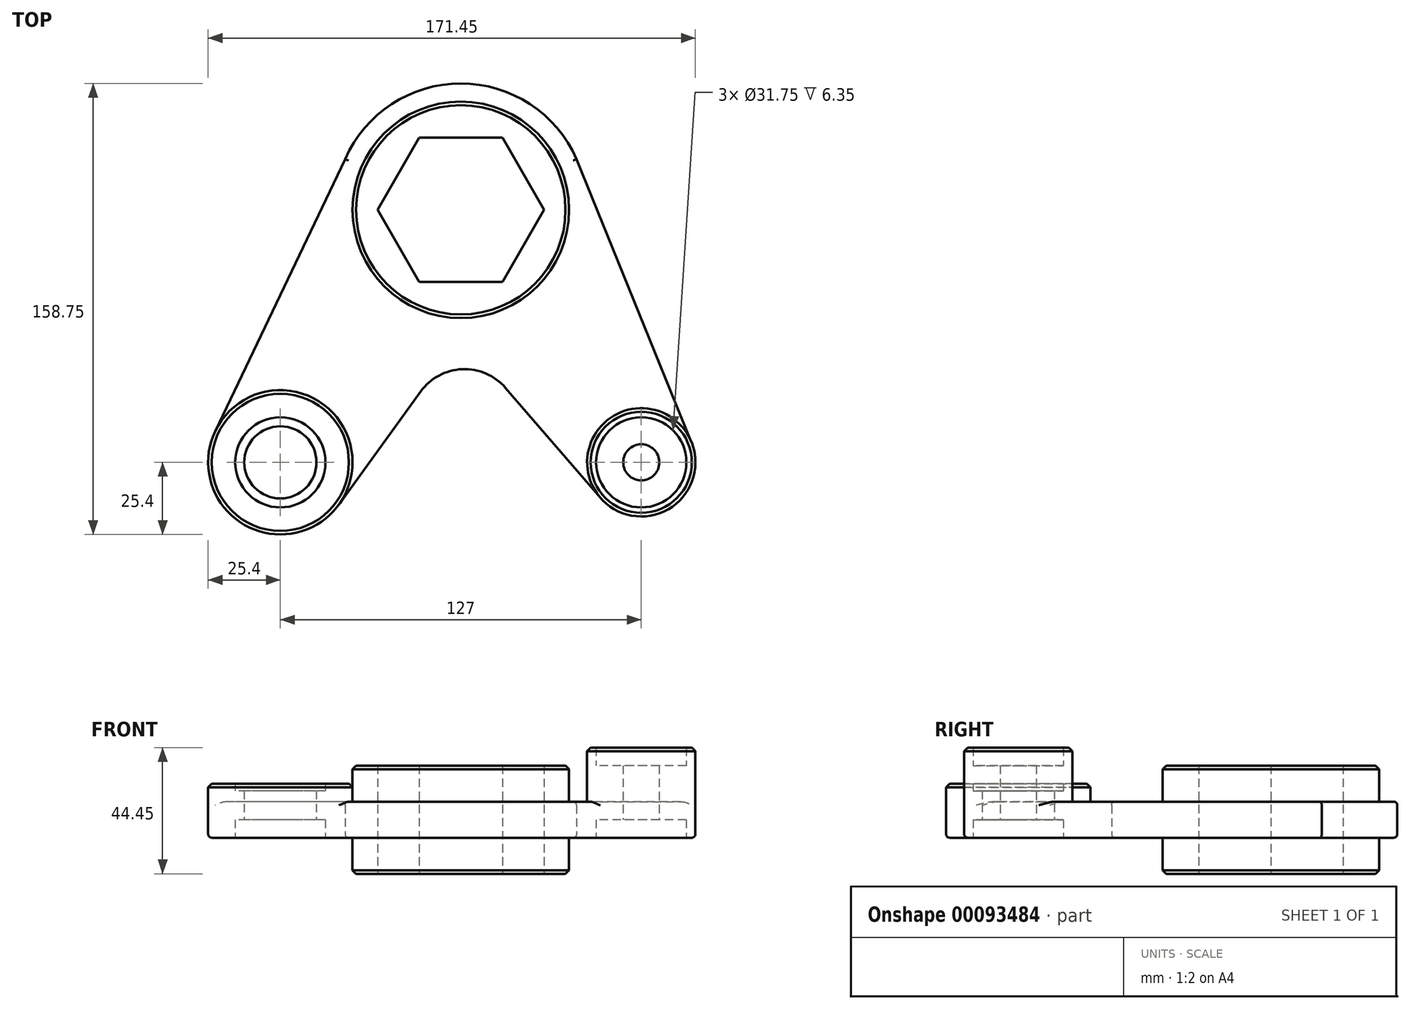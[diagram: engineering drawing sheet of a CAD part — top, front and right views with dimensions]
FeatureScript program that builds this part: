
annotation { "Feature Type Name" : "Feature", "Feature Type Description" : "" }
export const myFeature = defineFeature(function(context is Context, id is Id, definition is map)
    precondition{}
    {
        {
            var Q0;
            Q0=qCreatedBy(makeId("Top.planeOp"),FACE);
            var sketch = newSketch(context, id + "F0", { "sketchPlane" : qUnion([Q0])});
            skCircle(sketch, "E0", {"center": v(0, 0) * mm, "radius": 38.1 * mm});
            skCircle(sketch, "E1", {"center": v(0, 0) * mm, "radius": 44.45 * mm});
            skArc(sketch, "E2", {"start": v(-38.1, -88.9) * mm, "mid": v(-87.67, -81.08) * mm, "end": v(-42.92, -103.79) * mm});
            skCircle(sketch, "E3", {"center": v(63.5, -88.9) * mm, "radius": 19.05 * mm});
            skLineSegment(sketch, "E4", {"start": v(-40.71, 17.84) * mm, "end": v(-86.42, -77.96) * mm});
            skLineSegment(sketch, "E5", {"start": v(40.71, 17.84) * mm, "end": v(81.15, -81.73) * mm});
            skLineSegment(sketch, "E6", {"start": v(-14.12, -63.97) * mm, "end": v(-42.92, -103.79) * mm});
            skLineSegment(sketch, "E7", {"start": v(15.74, -62.7) * mm, "end": v(49.08, -101.34) * mm});
            skPoint(sketch, "E8.visualSharp", {"position": v(0, -44.45) * mm});
            skArc(sketch, "E8.filletArc", {"start": v(15.74, -62.7) * mm, "mid": v(0.5, -56.1) * mm, "end": v(-14.12, -63.97) * mm});
            skCircle(sketch, "E9.cCircle", {"center": v(0, 0) * mm, "radius": 25.4 * mm, "construction": true});
            skLineSegment(sketch, "E9.0", {"start": v(-14.66, 25.4) * mm, "end": v(14.66, 25.4) * mm});
            skLineSegment(sketch, "E9.1", {"start": v(14.66, 25.4) * mm, "end": v(29.33, 0) * mm});
            skLineSegment(sketch, "E9.2", {"start": v(29.33, 0) * mm, "end": v(14.66, -25.4) * mm});
            skLineSegment(sketch, "E9.3", {"start": v(14.66, -25.4) * mm, "end": v(-14.66, -25.4) * mm});
            skLineSegment(sketch, "E9.4", {"start": v(-14.66, -25.4) * mm, "end": v(-29.33, 0) * mm});
            skLineSegment(sketch, "E9.5", {"start": v(-29.33, 0) * mm, "end": v(-14.66, 25.4) * mm});
            skPoint(sketch, "E9.0.midPoint", {"position": v(0, 25.4) * mm});
            skCircle(sketch, "E10", {"center": v(63.5, -88.9) * mm, "radius": 6.35 * mm});
            skCircle(sketch, "E11", {"center": v(63.5, -88.9) * mm, "radius": 15.88 * mm});
            skCircle(sketch, "E12", {"center": v(-63.5, -88.9) * mm, "radius": 12.7 * mm});
            skCircle(sketch, "E13", {"center": v(-63.5, -88.9) * mm, "radius": 15.88 * mm});
            skArc(sketch, "E14", {"start": v(-86.42, -77.96) * mm, "mid": v(-69.1, -113.67) * mm, "end": v(-38.1, -88.9) * mm});
            skSolve(sketch);
        }
        {
            var Q0;
            {var subQ0=sQuery(id+"F0.wireOp",EDGE,"E4");Q0=makeQuery(id+"F0.imprint","IMPRINT",FACE,{"disambiguationData":[TD([[makeQuery(id+"F0.imprint","IMPRINT",EDGE,{"derivedFrom":subQ0}),1.0]])]});}
            var Q1;
            {var subQ0=sQuery(id+"F0.wireOp",EDGE,"E2");var subQ1=makeQuery(id+"F0.imprint","INTERSECT",VERTEX,{"derivedFrom":[subQ0,sQuery(id+"F0.wireOp",EDGE,"E4")]});Q1=makeQuery(id+"F0.imprint","IMPRINT",FACE,{"disambiguationData":[TD([[makeQuery(id+"F0.imprint","IMPRINT",EDGE,{"disambiguationData":[TD([[subQ1,-1.0]])],"derivedFrom":subQ0}),1.0]])]});}
            var Q2;
            {var subQ0=sQuery(id+"F0.wireOp",EDGE,"E3");var subQ1=makeQuery(id+"F0.imprint","INTERSECT",VERTEX,{"derivedFrom":[subQ0,sQuery(id+"F0.wireOp",EDGE,"E5")]});Q2=makeQuery(id+"F0.imprint","IMPRINT",FACE,{"disambiguationData":[TD([[makeQuery(id+"F0.imprint","IMPRINT",EDGE,{"disambiguationData":[TD([[subQ1,-1.0]])],"derivedFrom":subQ0}),1.0]])]});}
            var Q3;
            Q3=makeQuery(id+"F0.imprint","IMPRINT",FACE,{"disambiguationData":[TD([[makeQuery(id+"F0.imprint","IMPRINT",EDGE,{"derivedFrom":sQuery(id+"F0.wireOp",EDGE,"E0")}),-1.0]])]});
            extrude(context, id + "F1", {"entities" : qUnion([Q0, Q1, Q2, Q3]), "endBound" : BoundingType.SYMMETRIC, "depth" : 12.7 * mm});
        }
        {
            var Q0;
            Q0=makeQuery(id+"F0.imprint","IMPRINT",FACE,{"disambiguationData":[TD([[makeQuery(id+"F0.imprint","IMPRINT",EDGE,{"derivedFrom":sQuery(id+"F0.wireOp",EDGE,"E0")}),1.0]])]});
            extrude(context, id + "F2", {"entities" : qUnion([Q0]), "operationType" : NewBodyOperationType.ADD, "endBound" : BoundingType.SYMMETRIC, "depth" : 38.1 * mm});
        }
        {
            var Q0;
            {var subQ0=sQuery(id+"F0.wireOp",EDGE,"E3");var subQ1=makeQuery(id+"F0.imprint","INTERSECT",VERTEX,{"derivedFrom":[subQ0,sQuery(id+"F0.wireOp",EDGE,"E5")]});Q0=makeQuery(id+"F0.imprint","IMPRINT",FACE,{"disambiguationData":[TD([[makeQuery(id+"F0.imprint","IMPRINT",EDGE,{"disambiguationData":[TD([[subQ1,-1.0]])],"derivedFrom":subQ0}),1.0]])]});}
            extrude(context, id + "F3", {"entities" : qUnion([Q0]), "operationType" : NewBodyOperationType.ADD, "depth" : 25.4 * mm});
        }
        {
            var Q0;
            {var subQ0=sQuery(id+"F0.wireOp",EDGE,"E2");var subQ1=makeQuery(id+"F0.imprint","INTERSECT",VERTEX,{"derivedFrom":[subQ0,sQuery(id+"F0.wireOp",EDGE,"E4")]});Q0=makeQuery(id+"F0.imprint","IMPRINT",FACE,{"disambiguationData":[TD([[makeQuery(id+"F0.imprint","IMPRINT",EDGE,{"disambiguationData":[TD([[subQ1,-1.0]])],"derivedFrom":subQ0}),1.0]])]});}
            extrude(context, id + "F4", {"entities" : qUnion([Q0]), "operationType" : NewBodyOperationType.ADD, "depth" : 12.7 * mm});
        }
        {
            var Q0;
            Q0=makeQuery(id+"F0.imprint","IMPRINT",FACE,{"disambiguationData":[TD([[makeQuery(id+"F0.imprint","IMPRINT",EDGE,{"derivedFrom":sQuery(id+"F0.wireOp",EDGE,"E10")}),-1.0]])]});
            extrude(context, id + "F5", {"entities" : qUnion([Q0]), "operationType" : NewBodyOperationType.ADD, "depth" : 19.05 * mm});
        }
        {
            var Q0;
            Q0=makeQuery(id+"F0.imprint","IMPRINT",FACE,{"disambiguationData":[TD([[makeQuery(id+"F0.imprint","IMPRINT",EDGE,{"derivedFrom":sQuery(id+"F0.wireOp",EDGE,"E12")}),-1.0]])]});
            extrude(context, id + "F6", {"entities" : qUnion([Q0]), "operationType" : NewBodyOperationType.ADD, "depth" : 10.16 * mm});
        }
        {
            var Q0;
            Q0=makeQuery(id+"F2.opExtrude","CAP_EDGE",EDGE,{"disambiguationData":[OSD([sQuery(id+"F0.wireOp",EDGE,"E0")])],"isStart":true});
            var Q1;
            Q1=makeQuery(id+"F2.opExtrude","CAP_EDGE",EDGE,{"disambiguationData":[OSD([sQuery(id+"F0.wireOp",EDGE,"E0")])],"isStart":false});
            var Q2;
            Q2=makeQuery(id+"F4.opExtrude","CAP_EDGE",EDGE,{"disambiguationData":[OSD([sQuery(id+"F0.wireOp",EDGE,"E2")])],"isStart":false});
            var Q3;
            Q3=makeQuery(id+"F3.opExtrude","CAP_EDGE",EDGE,{"disambiguationData":[OSD([sQuery(id+"F0.wireOp",EDGE,"E3")])],"isStart":false});
            chamfer(context, id + "F7", {"entities" : qUnion([Q0, Q1, Q2, Q3]), "width" : 1.27 * mm, "tangentPropagation" : true});
        }
        {
            var Q0;
            Q0=makeQuery(id+"F1.opExtrude","CAP_EDGE",EDGE,{"disambiguationData":[OSD([sQuery(id+"F0.wireOp",EDGE,"E4")])],"isStart":false});
            var Q1;
            Q1=makeQuery(id+"F1.opExtrude","CAP_EDGE",EDGE,{"disambiguationData":[OSD([sQuery(id+"F0.wireOp",EDGE,"E1")])],"isStart":false});
            var Q2;
            Q2=makeQuery(id+"F1.opExtrude","CAP_EDGE",EDGE,{"disambiguationData":[OSD([sQuery(id+"F0.wireOp",EDGE,"E5")])],"isStart":false});
            var Q3;
            Q3=makeQuery(id+"F1.opExtrude","CAP_EDGE",EDGE,{"disambiguationData":[OSD([sQuery(id+"F0.wireOp",EDGE,"E7")])],"isStart":false});
            var Q4;
            Q4=makeQuery(id+"F1.opExtrude","CAP_EDGE",EDGE,{"disambiguationData":[OSD([sQuery(id+"F0.wireOp",EDGE,"E8.filletArc")])],"isStart":false});
            var Q5;
            Q5=makeQuery(id+"F1.opExtrude","CAP_EDGE",EDGE,{"disambiguationData":[OSD([sQuery(id+"F0.wireOp",EDGE,"E6")])],"isStart":false});
            var Q6;
            Q6=makeQuery(id+"F1.opExtrude","CAP_EDGE",EDGE,{"disambiguationData":[OSD([sQuery(id+"F0.wireOp",EDGE,"E4")])],"isStart":true});
            var Q7;
            Q7=makeQuery(id+"F1.opExtrude","CAP_EDGE",EDGE,{"disambiguationData":[OSD([sQuery(id+"F0.wireOp",EDGE,"E1")])],"isStart":true});
            var Q8;
            Q8=makeQuery(id+"F1.opExtrude","CAP_EDGE",EDGE,{"disambiguationData":[OSD([sQuery(id+"F0.wireOp",EDGE,"E5")])],"isStart":true});
            fillet(context, id + "F8", {"entities" : qUnion([Q0, Q1, Q2, Q3, Q4, Q5, Q6, Q7, Q8]), "radius" : 1.27 * mm, "tangentPropagation" : true, "allowEdgeOverflow" : false});
        }
    });
